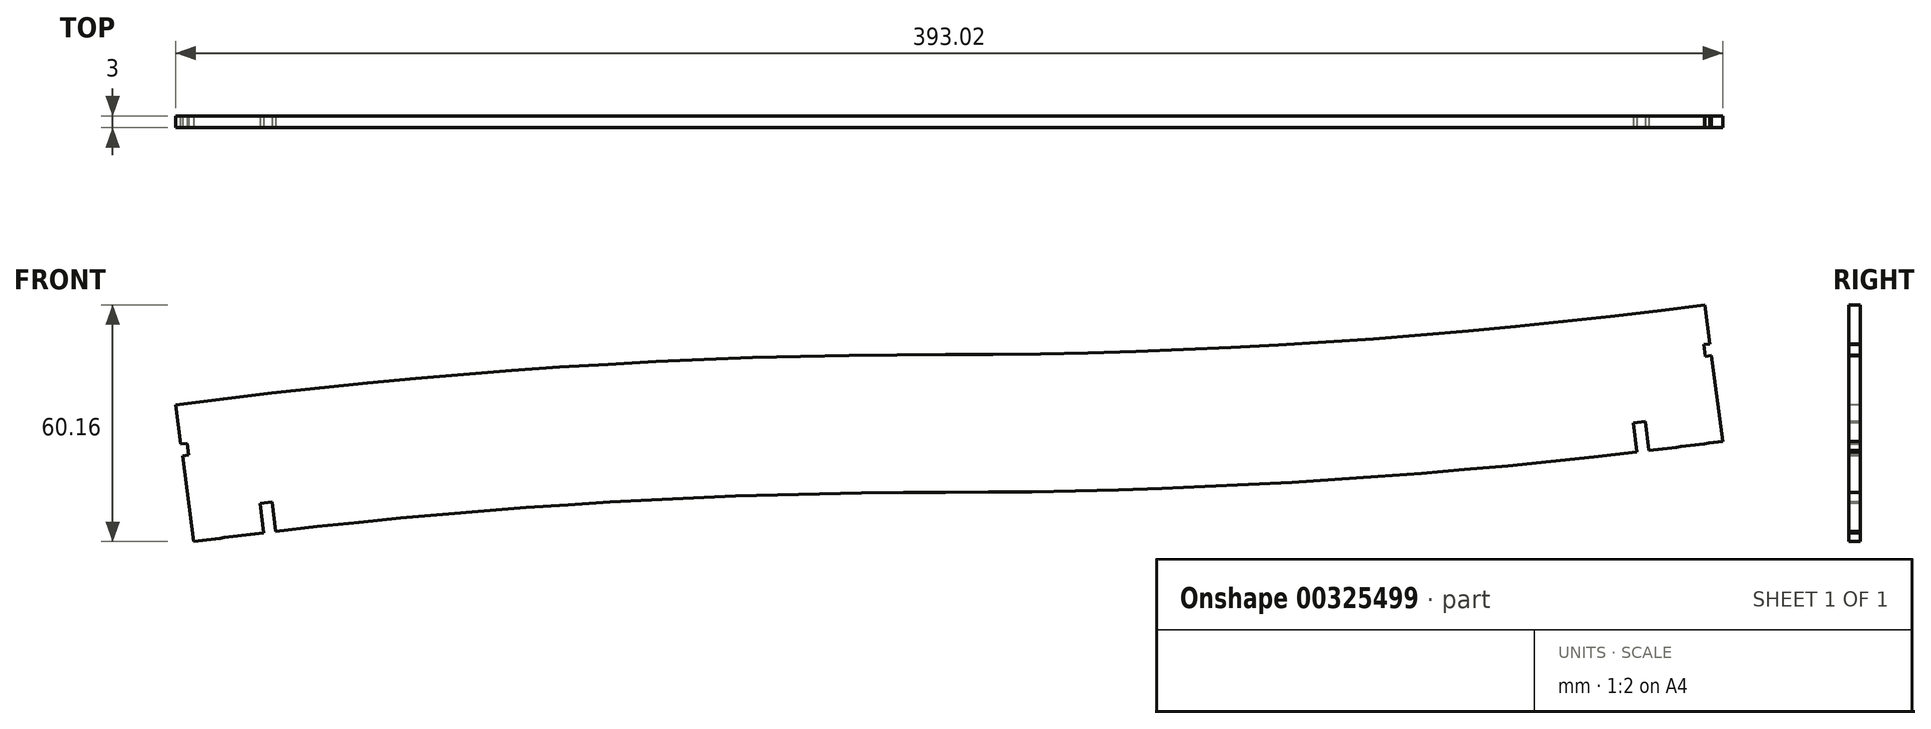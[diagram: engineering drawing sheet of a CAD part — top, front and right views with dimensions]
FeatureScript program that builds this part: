
annotation { "Feature Type Name" : "Feature", "Feature Type Description" : "" }
export const myFeature = defineFeature(function(context is Context, id is Id, definition is map)
    precondition{}
    {
        {
            var Q0;
            Q0=qCreatedBy(makeId("Front.planeOp"),FACE);
            var sketch = newSketch(context, id + "F0", { "sketchPlane" : qUnion([Q0])});
            skCircle(sketch, "E0", {"center": v(0, -1488) * mm, "radius": 1488 * mm, "construction": true});
            skCircle(sketch, "E1", {"center": v(0, 1488) * mm, "radius": 1488 * mm, "construction": true});
            skLineSegment(sketch, "E2", {"start": v(0, -1488) * mm, "end": v(0, 1488) * mm, "construction": true});
            skLineSegment(sketch, "E3", {"start": v(0, -1488) * mm, "end": v(-385.12, -50.7) * mm, "construction": true});
            skLineSegment(sketch, "E4", {"start": v(0, 1488) * mm, "end": v(385.12, 50.7) * mm, "construction": true});
            skArc(sketch, "E5", {"start": v(-385.12, -50.7) * mm, "mid": v(-194.22, -12.73) * mm, "end": v(0, 0) * mm, "construction": true});
            skArc(sketch, "E6", {"start": v(0, 0) * mm, "mid": v(194.22, 12.73) * mm, "end": v(385.12, 50.7) * mm, "construction": true});
            skArc(sketch, "E7", {"start": v(-194.22, -12.73) * mm, "mid": v(-97.32, -3.19) * mm, "end": v(0, 0) * mm});
            skArc(sketch, "E8", {"start": v(0, 0) * mm, "mid": v(97.32, 3.19) * mm, "end": v(194.22, 12.73) * mm});
            skSolve(sketch);
        }
        {
            var Q0;
            Q0=qCreatedBy(makeId("Right.planeOp"),FACE);
            var sketch = newSketch(context, id + "F1", { "sketchPlane" : qUnion([Q0])});
            skLineSegment(sketch, "E9.bottom", {"start": v(0, 10) * mm, "end": v(-3, 10) * mm});
            skLineSegment(sketch, "E9.top", {"start": v(0, -25) * mm, "end": v(-3, -25) * mm});
            skLineSegment(sketch, "E9.left", {"start": v(0, 10) * mm, "end": v(0, -25) * mm});
            skLineSegment(sketch, "E9.right", {"start": v(-3, 10) * mm, "end": v(-3, -25) * mm});
            skSolve(sketch);
        }
        {
            var Q0;
            Q0 = qSketchRegion(id + "F1", true);
            var Q1;
            Q1=sQuery(id+"F0.wireOp",EDGE,"E7");
            sweep(context, id + "F2", {"profiles" : qUnion([Q0]), "path" : qUnion([Q1])});
        }
        {
            var Q0;
            Q0 = qSketchRegion(id + "F1", true);
            var Q1;
            Q1=sQuery(id+"F0.wireOp",EDGE,"E8");
            sweep(context, id + "F3", {"operationType" : NewBodyOperationType.ADD, "profiles" : qUnion([Q0]), "path" : qUnion([Q1])});
        }
        {
            var Q0;
            Q0=qCreatedBy(makeId("Front.planeOp"),FACE);
            var sketch = newSketch(context, id + "F4", { "sketchPlane" : qUnion([Q0])});
            skLineSegment(sketch, "E10.0", {"start": v(0, -1488) * mm, "end": v(0, 1488) * mm, "construction": true});
            skLineSegment(sketch, "E11.0", {"start": v(192.92, 22.64) * mm, "end": v(197.49, -12.06) * mm});
            skLineSegment(sketch, "E12", {"start": v(192.67, 12.53) * mm, "end": v(195.78, 12.94) * mm});
            skLineSegment(sketch, "E13", {"start": v(195.78, 12.94) * mm, "end": v(196.17, 9.96) * mm});
            skLineSegment(sketch, "E14", {"start": v(196.17, 9.96) * mm, "end": v(193.06, 9.55) * mm});
            skLineSegment(sketch, "E15", {"start": v(193.06, 9.55) * mm, "end": v(192.67, 12.53) * mm});
            skPoint(sketch, "E16", {"position": v(194.22, 12.73) * mm});
            skPoint(sketch, "E17", {"position": v(194.61, 9.76) * mm});
            skSolve(sketch);
        }
        {
            var Q0;
            Q0 = qSketchRegion(id + "F4", true);
            extrude(context, id + "F5", {"entities" : qUnion([Q0]), "operationType" : NewBodyOperationType.REMOVE, "endBound" : BoundingType.UP_TO_NEXT, "depth" : 25 * mm});
        }
        {
            var Q0;
            {var subQ0=sQuery(id+"F1.wireOp",EDGE,"E9.right");Q0=makeQuery(id+"F3.boolean.opBoolean","MERGE",FACE,{"derivedFrom":[makeQuery(id+"F2.opSweep","SWEPT_FACE",FACE,{"disambiguationData":[OSD([sQuery(id+"F0.wireOp",EDGE,"E7"),subQ0])]}),makeQuery(id+"F3.opSweep","SWEPT_FACE",FACE,{"disambiguationData":[OSD([sQuery(id+"F0.wireOp",EDGE,"E8"),subQ0])]})]});}
            var sketch = newSketch(context, id + "F6", { "sketchPlane" : qUnion([Q0])});
            skLineSegment(sketch, "E18", {"start": v(-195.78, -12.94) * mm, "end": v(-192.67, -12.53) * mm});
            skLineSegment(sketch, "E19", {"start": v(-192.67, -12.53) * mm, "end": v(-192.27, -15.5) * mm});
            skLineSegment(sketch, "E20", {"start": v(-192.27, -15.5) * mm, "end": v(-195.39, -15.9) * mm});
            skLineSegment(sketch, "E21", {"start": v(-195.39, -15.9) * mm, "end": v(-195.78, -12.94) * mm});
            skLineSegment(sketch, "E22", {"start": v(-193.83, -15.7) * mm, "end": v(-194.22, -12.73) * mm, "construction": true});
            skSolve(sketch);
        }
        {
            var Q0;
            Q0 = qSketchRegion(id + "F6", true);
            var Q1;
            {var subQ0=sQuery(id+"F1.wireOp",EDGE,"E9.left");Q1=makeQuery(id+"F3.boolean.opBoolean","MERGE",FACE,{"derivedFrom":[makeQuery(id+"F2.opSweep","SWEPT_FACE",FACE,{"disambiguationData":[OSD([sQuery(id+"F0.wireOp",EDGE,"E7"),subQ0])]}),makeQuery(id+"F3.opSweep","SWEPT_FACE",FACE,{"disambiguationData":[OSD([sQuery(id+"F0.wireOp",EDGE,"E8"),subQ0])]})]});}
            extrude(context, id + "F7", {"entities" : qUnion([Q0]), "operationType" : NewBodyOperationType.REMOVE, "endBound" : BoundingType.UP_TO_SURFACE, "oppositeDirection" : true, "endBoundEntityFace" : qUnion([Q1]), "depth" : 25 * mm});
        }
        {
            var Q0;
            {var subQ0=sQuery(id+"F1.wireOp",EDGE,"E9.right");Q0=makeQuery(id+"F3.boolean.opBoolean","MERGE",FACE,{"derivedFrom":[makeQuery(id+"F2.opSweep","SWEPT_FACE",FACE,{"disambiguationData":[OSD([sQuery(id+"F0.wireOp",EDGE,"E7"),subQ0])]}),makeQuery(id+"F3.opSweep","SWEPT_FACE",FACE,{"disambiguationData":[OSD([sQuery(id+"F0.wireOp",EDGE,"E8"),subQ0])]})]});}
            var sketch = newSketch(context, id + "F8", { "sketchPlane" : qUnion([Q0])});
            skCircle(sketch, "E23", {"center": v(0, -1488) * mm, "radius": 1463 * mm, "construction": true});
            skLineSegment(sketch, "E24", {"start": v(-174.05, -27.84) * mm, "end": v(-173.17, -35.29) * mm});
            skLineSegment(sketch, "E25", {"start": v(-173.17, -35.29) * mm, "end": v(-170.2, -34.93) * mm});
            skLineSegment(sketch, "E26", {"start": v(-170.2, -34.93) * mm, "end": v(-171.07, -27.48) * mm});
            skLineSegment(sketch, "E27", {"start": v(-171.07, -27.48) * mm, "end": v(-174.05, -27.84) * mm});
            skLineSegment(sketch, "E28", {"start": v(-172.56, -27.66) * mm, "end": v(-171.68, -35.1) * mm, "construction": true});
            skLineSegment(sketch, "E29.0", {"start": v(-190.96, -37.52) * mm, "end": v(-193.83, -15.7) * mm, "construction": true});
            skArc(sketch, "E30", {"start": v(-172.12, -31.38) * mm, "mid": v(-181.79, -32.56) * mm, "end": v(-191.45, -33.8) * mm, "construction": true});
            skSolve(sketch);
        }
        {
            var Q0;
            Q0 = qSketchRegion(id + "F8", true);
            extrude(context, id + "F9", {"entities" : qUnion([Q0]), "operationType" : NewBodyOperationType.REMOVE, "endBound" : BoundingType.UP_TO_NEXT, "oppositeDirection" : true, "depth" : 25 * mm});
        }
        {
            var Q0;
            {var subQ0=sQuery(id+"F1.wireOp",EDGE,"E9.right");Q0=makeQuery(id+"F3.boolean.opBoolean","MERGE",FACE,{"derivedFrom":[makeQuery(id+"F2.opSweep","SWEPT_FACE",FACE,{"disambiguationData":[OSD([sQuery(id+"F0.wireOp",EDGE,"E7"),subQ0])]}),makeQuery(id+"F3.opSweep","SWEPT_FACE",FACE,{"disambiguationData":[OSD([sQuery(id+"F0.wireOp",EDGE,"E8"),subQ0])]})]});}
            var sketch = newSketch(context, id + "F10", { "sketchPlane" : qUnion([Q0])});
            skLineSegment(sketch, "E31", {"start": v(175.75, -15.26) * mm, "end": v(174.8, -7.32) * mm});
            skLineSegment(sketch, "E32", {"start": v(174.8, -7.32) * mm, "end": v(177.79, -6.97) * mm});
            skLineSegment(sketch, "E33", {"start": v(177.79, -6.97) * mm, "end": v(178.73, -14.91) * mm});
            skLineSegment(sketch, "E34", {"start": v(178.73, -14.91) * mm, "end": v(175.75, -15.26) * mm});
            skLineSegment(sketch, "E35", {"start": v(176.3, -7.14) * mm, "end": v(177.24, -15.09) * mm, "construction": true});
            skArc(sketch, "E36", {"start": v(176.3, -7.14) * mm, "mid": v(186.4, -5.91) * mm, "end": v(196.5, -4.62) * mm, "construction": true});
            skSolve(sketch);
        }
        {
            var Q0;
            Q0 = qSketchRegion(id + "F10", true);
            var Q1;
            {var subQ0=sQuery(id+"F1.wireOp",EDGE,"E9.left");Q1=makeQuery(id+"F3.boolean.opBoolean","MERGE",FACE,{"derivedFrom":[makeQuery(id+"F2.opSweep","SWEPT_FACE",FACE,{"disambiguationData":[OSD([sQuery(id+"F0.wireOp",EDGE,"E7"),subQ0])]}),makeQuery(id+"F3.opSweep","SWEPT_FACE",FACE,{"disambiguationData":[OSD([sQuery(id+"F0.wireOp",EDGE,"E8"),subQ0])]})]});}
            extrude(context, id + "F11", {"entities" : qUnion([Q0]), "operationType" : NewBodyOperationType.REMOVE, "endBound" : BoundingType.UP_TO_NEXT, "oppositeDirection" : true, "endBoundEntityFace" : qUnion([Q1]), "depth" : 25 * mm});
        }
    });
